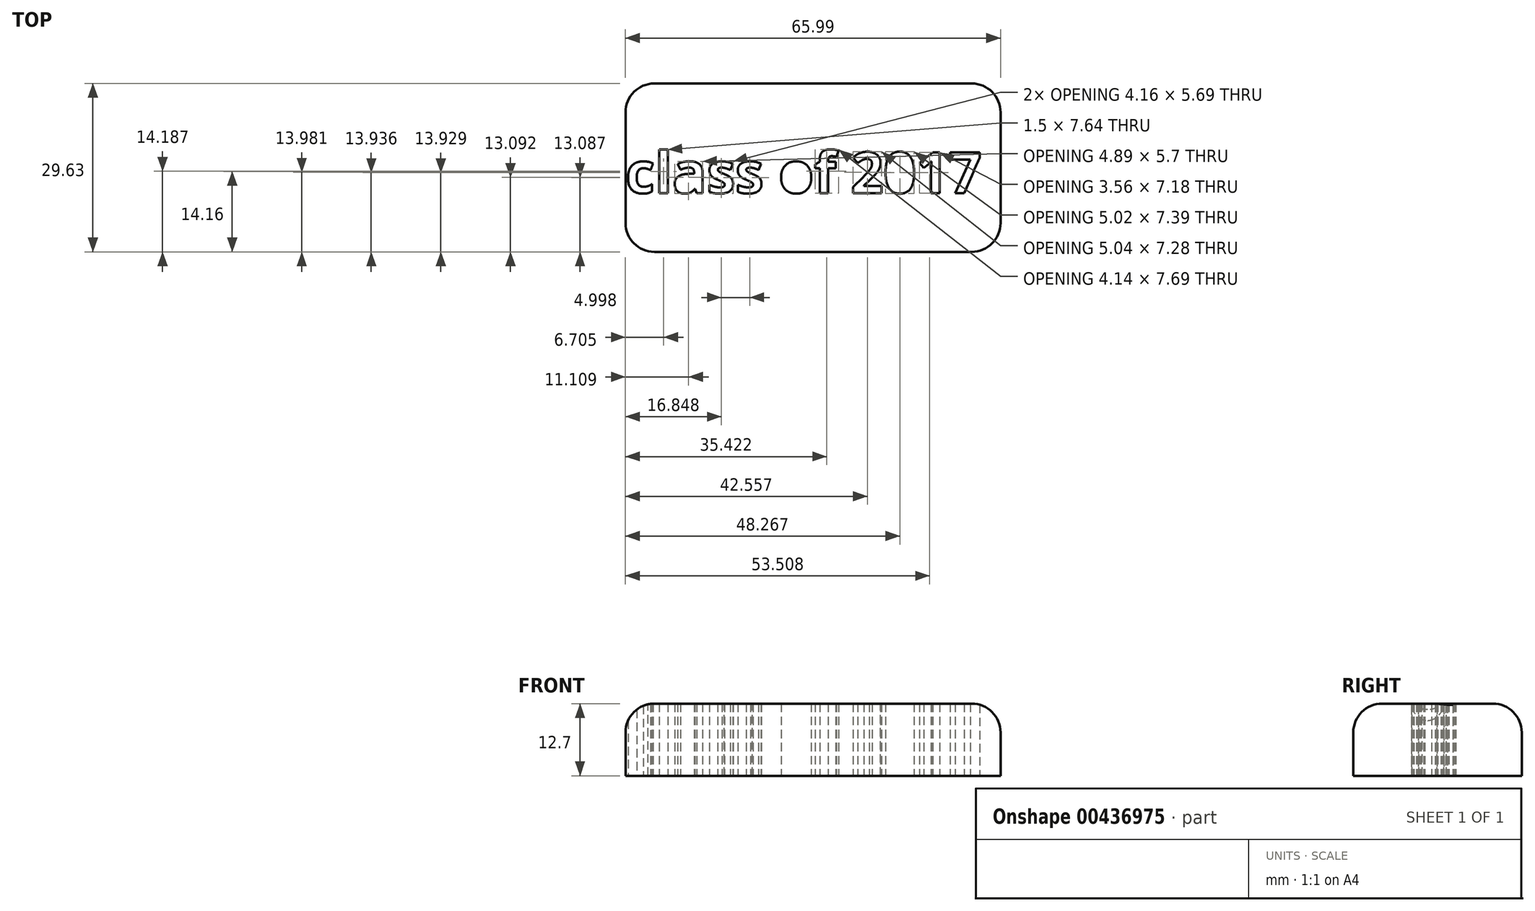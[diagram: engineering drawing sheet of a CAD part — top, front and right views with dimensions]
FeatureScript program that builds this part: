
annotation { "Feature Type Name" : "Feature", "Feature Type Description" : "" }
export const myFeature = defineFeature(function(context is Context, id is Id, definition is map)
    precondition{}
    {
        {
            var Q0;
            Q0=qCreatedBy(makeId("Top.planeOp"),FACE);
            var sketch = newSketch(context, id + "F0", { "sketchPlane" : qUnion([Q0])});
            skLineSegment(sketch, "E0.bottom", {"start": v(-65.99, 49.8) * mm, "end": v(0, 49.8) * mm});
            skLineSegment(sketch, "E0.top", {"start": v(-65.99, 20.16) * mm, "end": v(0, 20.16) * mm});
            skLineSegment(sketch, "E0.left", {"start": v(-65.99, 49.8) * mm, "end": v(-65.99, 20.16) * mm});
            skLineSegment(sketch, "E0.right", {"start": v(0, 49.8) * mm, "end": v(0, 20.16) * mm});
            skText(sketch, "E1", { "text": "class of 2017", "fontName": "OpenSans-Bold.ttf"});
            const initialGuessF0  = {"E1": [-0.06599, 0.0305, 1, 0, 0.00724]};
            skSetInitialGuess(sketch, initialGuessF0);
            skSolve(sketch);
        }
        {
            var Q0;
            Q0 = qSketchRegion(id + "F0", true);
            extrude(context, id + "F1", {"entities" : qUnion([Q0]), "depth" : 12.7 * mm});
        }
        {
            var Q0;
            Q0=makeQuery(id+"F1.opExtrude","SWEPT_EDGE",EDGE,{"disambiguationData":[OSD([sQuery(id+"F0.wireOp",EDGE,"E0.bottom"),sQuery(id+"F0.wireOp",EDGE,"E0.left")])]});
            var Q1;
            Q1=makeQuery(id+"F1.opExtrude","CAP_EDGE",EDGE,{"disambiguationData":[OSD([sQuery(id+"F0.wireOp",EDGE,"E0.left")])],"isStart":false});
            var Q2;
            Q2=makeQuery(id+"F1.opExtrude","SWEPT_EDGE",EDGE,{"disambiguationData":[OSD([sQuery(id+"F0.wireOp",EDGE,"E0.top"),sQuery(id+"F0.wireOp",EDGE,"E0.left")])]});
            var Q3;
            Q3=makeQuery(id+"F1.opExtrude","CAP_EDGE",EDGE,{"disambiguationData":[OSD([sQuery(id+"F0.wireOp",EDGE,"E0.bottom")])],"isStart":false});
            var Q4;
            Q4=makeQuery(id+"F1.opExtrude","SWEPT_EDGE",EDGE,{"disambiguationData":[OSD([sQuery(id+"F0.wireOp",EDGE,"E0.bottom"),sQuery(id+"F0.wireOp",EDGE,"E0.right")])]});
            var Q5;
            Q5=makeQuery(id+"F1.opExtrude","CAP_EDGE",EDGE,{"disambiguationData":[OSD([sQuery(id+"F0.wireOp",EDGE,"E0.top")])],"isStart":false});
            var Q6;
            Q6=makeQuery(id+"F1.opExtrude","SWEPT_EDGE",EDGE,{"disambiguationData":[OSD([sQuery(id+"F0.wireOp",EDGE,"E0.top"),sQuery(id+"F0.wireOp",EDGE,"E0.right")])]});
            var Q7;
            Q7=makeQuery(id+"F1.opExtrude","CAP_EDGE",EDGE,{"disambiguationData":[OSD([sQuery(id+"F0.wireOp",EDGE,"E0.right")])],"isStart":false});
            fillet(context, id + "F2", {"entities" : qUnion([Q0, Q1, Q2, Q3, Q4, Q5, Q6, Q7]), "radius" : 5.08 * mm, "tangentPropagation" : true, "allowEdgeOverflow" : false});
        }
    });
